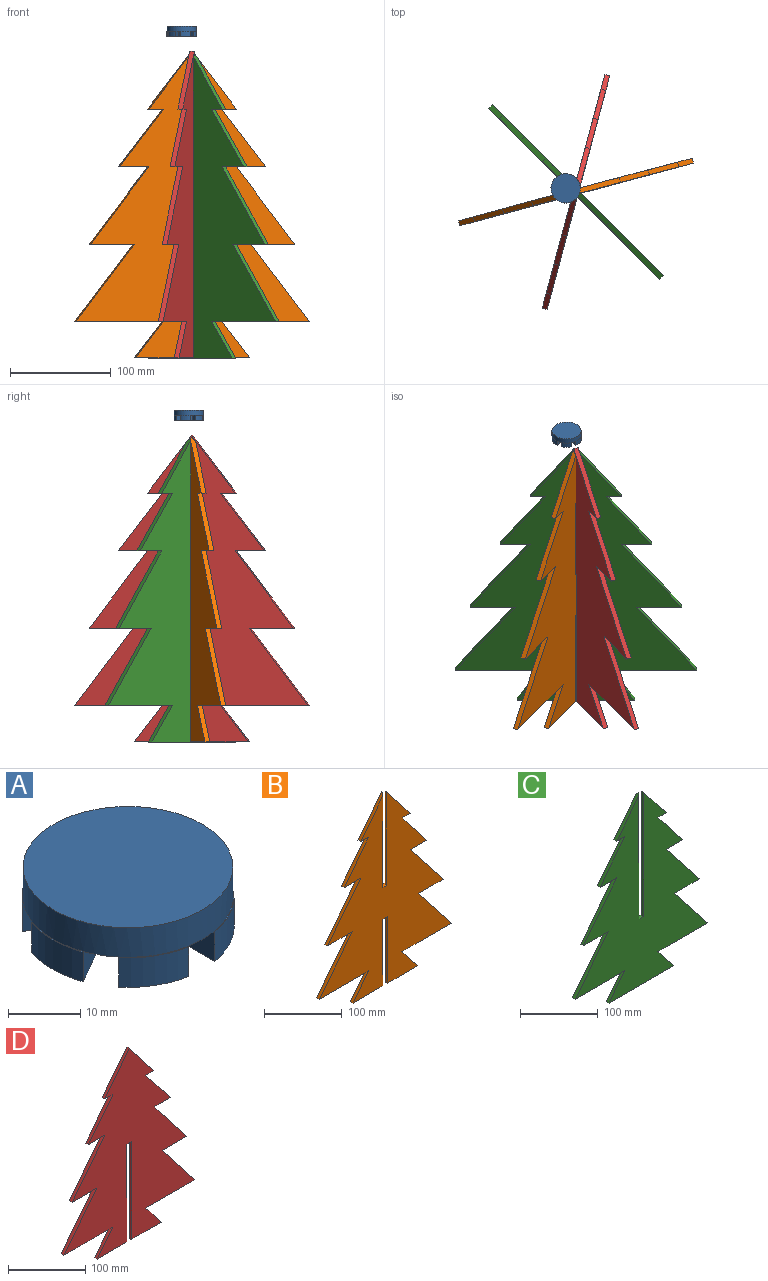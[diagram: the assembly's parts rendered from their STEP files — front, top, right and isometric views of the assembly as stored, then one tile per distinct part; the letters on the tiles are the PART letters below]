
ASSEMBLY  parts=4 mates=3
PART A: 33 faces, bbox 29.3x29x10 mm
  f0: plane 8.66x5.07mm, normal (0,0,1), area 1.4mm2, adj f1,f2,f3,f31
  f1: plane 10x5mm, normal (1,0,0), area 50mm2, adj f0,f2,f3,f4,f5
  f2: plane 8.66x5mm, normal (-0.5,0.87,0), area 50mm2, adj f0,f1,f3,f4,f5
  f3: cylinder r=14.64mm len=8.66mm, axis (0,0,-1), area 51mm2, adj f0,f1,f2,f4
  f4: plane 10x8.66mm, normal (0,0,-1), area 49.2mm2, adj f1,f2,f3
  f5: plane 29x27.27mm, normal (0,0,-1), area 373.8mm2, adj f1,f2,f7,f8,f12,f13,f17,f18
  f6: plane 10x1mm, normal (0,0,1), area 1.4mm2, adj f7,f8,f9,f31
  f7: plane 8.66x5mm, normal (0.5,-0.87,0), area 50mm2, adj f5,f6,f8,f9,f10
  f8: plane 8.66x5mm, normal (0.5,0.87,0), area 50mm2, adj f5,f6,f7,f9,f10
  f9: cylinder r=14.64mm len=10mm, axis (0,0,-1), area 51mm2, adj f6,f7,f8,f10
  f10: plane 10x9.54mm, normal (0,0,-1), area 49.2mm2, adj f7,f8,f9
  f11: plane 8.66x5.07mm, normal (0,0,1), area 1.4mm2, adj f12,f13,f14,f31
  f12: plane 8.66x5mm, normal (0.5,0.87,0), area 50mm2, adj f5,f11,f13,f14,f15
  f13: plane 10x5mm, normal (-1,0,0), area 50mm2, adj f5,f11,f12,f14,f15
  f14: cylinder r=14.64mm len=8.66mm, axis (0,0,-1), area 51mm2, adj f11,f12,f13,f15
  f15: plane 10x8.66mm, normal (0,0,-1), area 49.2mm2, adj f12,f13,f14
  f16: plane 10x1mm, normal (0,0,1), area 1.4mm2, adj f17,f18,f19,f31
  f17: plane 8.66x5mm, normal (-0.5,0.87,0), area 50mm2, adj f5,f16,f18,f19,f20
  f18: plane 8.66x5mm, normal (-0.5,-0.87,0), area 50mm2, adj f5,f16,f17,f19,f20
  f19: cylinder r=14.64mm len=10mm, axis (0,0,-1), area 51mm2, adj f16,f17,f18,f20
  f20: plane 10x9.54mm, normal (0,0,-1), area 49.2mm2, adj f17,f18,f19
  f21: plane 8.66x5.07mm, normal (0,0,1), area 1.4mm2, adj f22,f23,f24,f31
  f22: cylinder r=14.64mm len=8.66mm, axis (0,0,-1), area 51mm2, adj f21,f23,f24,f25
  f23: plane 10x5mm, normal (-1,0,0), area 50mm2, adj f5,f21,f22,f24,f25
  f24: plane 8.66x5mm, normal (0.5,-0.87,0), area 50mm2, adj f5,f21,f22,f23,f25
  f25: plane 10x8.66mm, normal (0,0,-1), area 49.2mm2, adj f22,f23,f24
  f26: plane 8.66x5mm, normal (-0.5,-0.87,0), area 50mm2, adj f5,f27,f28,f29,f30
  f27: plane 10x5mm, normal (1,0,0), area 50mm2, adj f5,f26,f28,f29,f30
  f28: cylinder r=14.64mm len=8.66mm, axis (0,0,-1), area 51mm2, adj f26,f27,f29,f30
  f29: plane 8.66x5.07mm, normal (0,0,1), area 1.4mm2, adj f26,f27,f28,f31
  f30: plane 10x8.66mm, normal (0,0,-1), area 49.2mm2, adj f26,f27,f28
  f31: cylinder r=14.5mm len=29mm, axis (0,0,-1), area 455.5mm2, adj f0,f5,f6,f11,f16,f21,f29,f32
  f32: plane 29x29mm, normal (0,0,1), area 660.5mm2, adj f31
PART B: 30 faces, bbox 240.3x5x303.1 mm
  f0: plane 55.69x5mm, normal (0,0,-1), area 274.8mm2, adj f1,f4,f13,f25,f28
  f1: plane 303.08x240.27mm, normal (0,1,0), area 35429.2mm2, adj f0,f2,f3,f5,f6,f7,f8,f9
  f2: plane 55.61x43.55mm, normal (0.79,0,0.62), area 341.5mm2, adj f1,f4,f5,f24
  f3: plane 55.61x43.55mm, normal (-0.79,0,0.62), area 341.5mm2, adj f1,f4,f6,f23
  f4: plane 303.08x240.27mm, normal (0,-1,0), area 35429.2mm2, adj f0,f2,f3,f5,f6,f7,f8,f9
  f5: plane 15.02x5mm, normal (0,0,-1), area 75.1mm2, adj f1,f2,f4,f21
  f6: plane 15.02x5mm, normal (0,0,-1), area 75.1mm2, adj f1,f3,f4,f7
  f7: plane 57.53x45.05mm, normal (-0.79,0,0.62), area 365.4mm2, adj f1,f4,f6,f8
  f8: plane 30.03x5mm, normal (0,0,-1), area 150.2mm2, adj f1,f4,f7,f9
  f9: plane 76.71x60.07mm, normal (-0.79,0,0.62), area 487.1mm2, adj f1,f4,f8,f10
  f10: plane 45.05x5mm, normal (0,0,-1), area 225.3mm2, adj f1,f4,f9,f11
  f11: plane 76.71x60.07mm, normal (-0.79,0,0.62), area 487.1mm2, adj f1,f4,f10,f12
  f12: plane 90.1x5mm, normal (0,0,-1), area 450.5mm2, adj f1,f4,f11,f13
  f13: plane 36.52x28.6mm, normal (-0.79,0,0.62), area 231.9mm2, adj f0,f1,f4,f12
  f14: plane 55.69x5mm, normal (0,0,-1), area 274.8mm2, adj f1,f4,f15,f26,f29
  f15: plane 36.52x28.6mm, normal (0.79,0,0.62), area 231.9mm2, adj f1,f4,f14,f16
  f16: plane 90.1x5mm, normal (0,0,-1), area 450.5mm2, adj f1,f4,f15,f17
  f17: plane 76.71x60.07mm, normal (0.79,0,0.62), area 487.1mm2, adj f1,f4,f16,f18
  f18: plane 45.05x5mm, normal (0,0,-1), area 225.3mm2, adj f1,f4,f17,f19
  f19: plane 76.71x60.07mm, normal (0.79,0,0.62), area 487.1mm2, adj f1,f4,f18,f20
  f20: plane 30.03x5mm, normal (0,0,-1), area 150.2mm2, adj f1,f4,f19,f21
  f21: plane 57.53x45.05mm, normal (0.79,0,0.62), area 365.4mm2, adj f1,f4,f5,f20
  f22: plane 8.78x5mm, normal (0,0,1), area 29.4mm2, adj f1,f4,f23,f24
  f23: plane 148.04x5mm, normal (0.87,-0.5,0), area 844.1mm2, adj f1,f3,f4,f22
  f24: plane 148.04x5mm, normal (-0.87,0.5,0), area 844.1mm2, adj f1,f2,f4,f22
  f25: plane 105x2.5mm, normal (0.87,0.5,0), area 303.1mm2, adj f0,f1,f27,f28
  f26: plane 105x2.5mm, normal (-0.87,0.5,0), area 303.1mm2, adj f1,f14,f27,f29
  f27: plane 8.78x5mm, normal (0,0,-1), area 36.7mm2, adj f1,f4,f25,f26,f28,f29
  f28: plane 105x2.5mm, normal (0.87,-0.5,0), area 303.1mm2, adj f0,f4,f25,f27
  f29: plane 105x2.5mm, normal (-0.87,-0.5,0), area 303.1mm2, adj f4,f14,f26,f27
PART C: 26 faces, bbox 240.3x5x301.2 mm
  f0: plane 299.4x240.27mm, normal (0,1,0), area 35489.8mm2, adj f1,f2,f3,f4,f5,f6,f7,f8
  f1: plane 15.02x5mm, normal (0,0,-1), area 75.1mm2, adj f0,f2,f19,f20
  f2: plane 53.77x42.11mm, normal (0.79,0,0.62), area 335.6mm2, adj f0,f1,f20,f22,f23
  f3: plane 53.77x42.11mm, normal (-0.79,0,0.62), area 335.6mm2, adj f0,f4,f20,f24,f25
  f4: plane 15.02x5mm, normal (0,0,-1), area 75.1mm2, adj f0,f3,f5,f20
  f5: plane 57.53x45.05mm, normal (-0.79,0,0.62), area 365.4mm2, adj f0,f4,f6,f20
  f6: plane 30.03x5mm, normal (0,0,-1), area 150.2mm2, adj f0,f5,f7,f20
  f7: plane 76.71x60.07mm, normal (-0.79,0,0.62), area 487.1mm2, adj f0,f6,f8,f20
  f8: plane 45.05x5mm, normal (0,0,-1), area 225.3mm2, adj f0,f7,f9,f20
  f9: plane 76.71x60.07mm, normal (-0.79,0,0.62), area 487.1mm2, adj f0,f8,f10,f20
  f10: plane 90.1x5mm, normal (0,0,-1), area 450.5mm2, adj f0,f9,f11,f20
  f11: plane 36.52x28.6mm, normal (-0.79,0,0.62), area 231.9mm2, adj f0,f10,f12,f20
  f12: plane 117.27x5mm, normal (0,0,-1), area 586.3mm2, adj f0,f11,f13,f20
  f13: plane 36.52x28.6mm, normal (0.79,0,0.62), area 231.9mm2, adj f0,f12,f14,f20
  f14: plane 90.1x5mm, normal (0,0,-1), area 450.5mm2, adj f0,f13,f15,f20
  f15: plane 76.71x60.07mm, normal (0.79,0,0.62), area 487.1mm2, adj f0,f14,f16,f20
  f16: plane 45.05x5mm, normal (0,0,-1), area 225.3mm2, adj f0,f15,f17,f20
  f17: plane 76.71x60.07mm, normal (0.79,0,0.62), area 487.1mm2, adj f0,f16,f18,f20
  f18: plane 30.03x5mm, normal (0,0,-1), area 150.2mm2, adj f0,f17,f19,f20
  f19: plane 57.53x45.05mm, normal (0.79,0,0.62), area 365.4mm2, adj f0,f1,f18,f20
  f20: plane 299.4x240.27mm, normal (0,-1,0), area 35489.8mm2, adj f1,f2,f3,f4,f5,f6,f7,f8
  f21: plane 8.78x5mm, normal (0,0,1), area 36.7mm2, adj f0,f20,f22,f23,f24,f25
  f22: plane 196.2x2.5mm, normal (-0.87,-0.5,0), area 563.7mm2, adj f2,f20,f21,f23
  f23: plane 196.2x2.5mm, normal (-0.87,0.5,0), area 563.7mm2, adj f0,f2,f21,f22
  f24: plane 196.2x2.5mm, normal (0.87,0.5,0), area 563.7mm2, adj f0,f3,f21,f25
  f25: plane 196.2x2.5mm, normal (0.87,-0.5,0), area 563.7mm2, adj f3,f20,f21,f24
PART D: 27 faces, bbox 240.3x5x305 mm
  f0: plane 55.69x5mm, normal (0,0,-1), area 274.8mm2, adj f1,f12,f21,f22,f25
  f1: plane 305x240.27mm, normal (0,1,0), area 35859.8mm2, adj f0,f2,f3,f4,f5,f6,f7,f8
  f2: plane 15.02x5mm, normal (0,0,-1), area 75.1mm2, adj f1,f3,f20,f21
  f3: plane 57.53x45.05mm, normal (0.79,0,0.62), area 365.4mm2, adj f1,f2,f4,f21
  f4: plane 57.53x45.05mm, normal (-0.79,0,0.62), area 365.4mm2, adj f1,f3,f5,f21
  f5: plane 15.02x5mm, normal (0,0,-1), area 75.1mm2, adj f1,f4,f6,f21
  f6: plane 57.53x45.05mm, normal (-0.79,0,0.62), area 365.4mm2, adj f1,f5,f7,f21
  f7: plane 30.03x5mm, normal (0,0,-1), area 150.2mm2, adj f1,f6,f8,f21
  f8: plane 76.71x60.07mm, normal (-0.79,0,0.62), area 487.1mm2, adj f1,f7,f9,f21
  f9: plane 45.05x5mm, normal (0,0,-1), area 225.3mm2, adj f1,f8,f10,f21
  f10: plane 76.71x60.07mm, normal (-0.79,0,0.62), area 487.1mm2, adj f1,f9,f11,f21
  f11: plane 90.1x5mm, normal (0,0,-1), area 450.5mm2, adj f1,f10,f12,f21
  f12: plane 36.52x28.6mm, normal (-0.79,0,0.62), area 231.9mm2, adj f0,f1,f11,f21
  f13: plane 55.69x5mm, normal (0,0,-1), area 274.8mm2, adj f1,f14,f21,f23,f26
  f14: plane 36.52x28.6mm, normal (0.79,0,0.62), area 231.9mm2, adj f1,f13,f15,f21
  f15: plane 90.1x5mm, normal (0,0,-1), area 450.5mm2, adj f1,f14,f16,f21
  f16: plane 76.71x60.07mm, normal (0.79,0,0.62), area 487.1mm2, adj f1,f15,f17,f21
  f17: plane 45.05x5mm, normal (0,0,-1), area 225.3mm2, adj f1,f16,f18,f21
  f18: plane 76.71x60.07mm, normal (0.79,0,0.62), area 487.1mm2, adj f1,f17,f19,f21
  f19: plane 30.03x5mm, normal (0,0,-1), area 150.2mm2, adj f1,f18,f20,f21
  f20: plane 57.53x45.05mm, normal (0.79,0,0.62), area 365.4mm2, adj f1,f2,f19,f21
  f21: plane 305x240.27mm, normal (0,-1,0), area 35859.8mm2, adj f0,f2,f3,f4,f5,f6,f7,f8
  f22: plane 155x2.5mm, normal (0.87,0.5,0), area 447.4mm2, adj f0,f1,f24,f25
  f23: plane 155x2.5mm, normal (-0.87,0.5,0), area 447.4mm2, adj f1,f13,f24,f26
  f24: plane 8.78x5mm, normal (0,0,-1), area 36.7mm2, adj f1,f21,f22,f23,f25,f26
  f25: plane 155x2.5mm, normal (0.87,-0.5,0), area 447.4mm2, adj f0,f21,f22,f24
  f26: plane 155x2.5mm, normal (-0.87,-0.5,0), area 447.4mm2, adj f13,f21,f23,f24
PLACE A rot(axis=(0,0,-1),15deg) t=(131.92,41.17,192.92)mm
PLACE B rot(axis=(0,0,1),15deg) t=(159.45,45.31,-0.64)mm
PLACE C rot(axis=(0,0,-1),45deg) t=(157.05,26.71,-0.68)mm fixed
PLACE D rot(axis=(0,0,1),75deg) t=(144.54,56.68,-0.6)mm
MATE fastened C.f20 <-> A.f18  axis (-0.71,-0.71,0) through (140.38,36.32,-4.58)mm
MATE revolute B.f22 <-> D.f24  axis (0,0,1) through (142.14,38.08,27.86)mm
MATE revolute C.f21 <-> B.f27  axis (0,0,1) through (142.14,38.08,-22.18)mm
